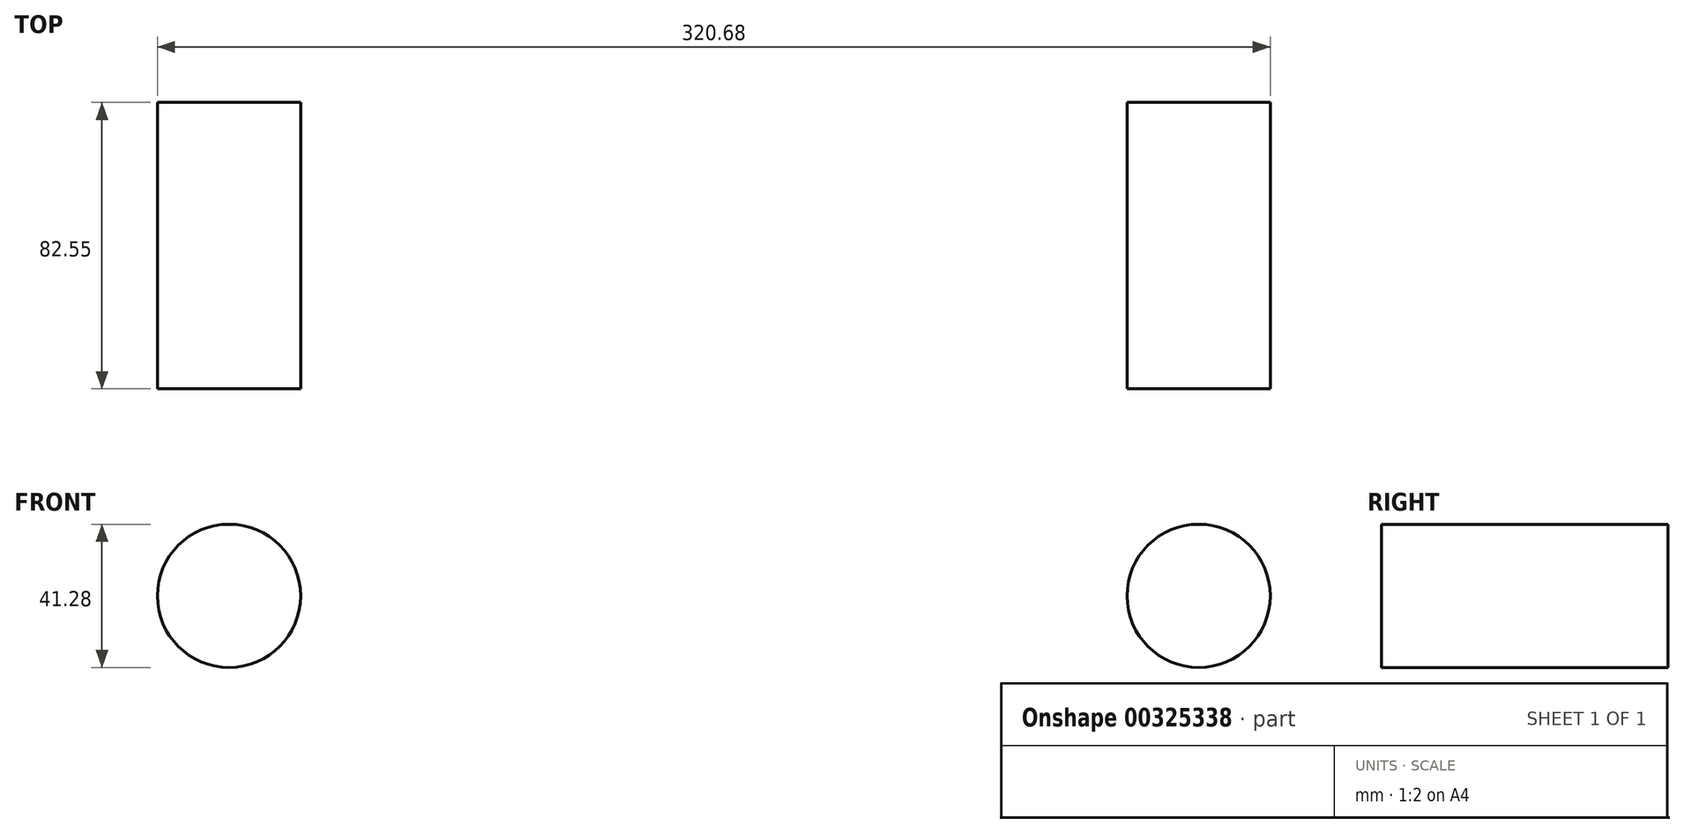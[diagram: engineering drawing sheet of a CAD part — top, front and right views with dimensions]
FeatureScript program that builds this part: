
annotation { "Feature Type Name" : "Feature", "Feature Type Description" : "" }
export const myFeature = defineFeature(function(context is Context, id is Id, definition is map)
    precondition{}
    {
        {
            var Q0;
            Q0=qCreatedBy(makeId("Top.planeOp"),FACE);
            var sketch = newSketch(context, id + "F0", { "sketchPlane" : qUnion([Q0])});
            skLineSegment(sketch, "E0", {"start": v(279.4, -82.55) * mm, "end": v(279.4, 0) * mm});
            skLineSegment(sketch, "E1", {"start": v(0, -82.55) * mm, "end": v(0, 0) * mm});
            skLineSegment(sketch, "E2.bottom", {"start": v(33.02, 67.89) * mm, "end": v(248.92, 67.89) * mm});
            skLineSegment(sketch, "E2.top", {"start": v(33.02, -100.77) * mm, "end": v(248.92, -100.77) * mm});
            skLineSegment(sketch, "E2.left", {"start": v(33.02, 67.89) * mm, "end": v(33.02, -100.77) * mm});
            skLineSegment(sketch, "E2.right", {"start": v(248.92, 67.89) * mm, "end": v(248.92, -100.77) * mm});
            skLineSegment(sketch, "E3.bottom", {"start": v(77.47, -367.47) * mm, "end": v(204.47, -367.47) * mm});
            skLineSegment(sketch, "E3.top", {"start": v(77.47, -549.3) * mm, "end": v(204.47, -549.3) * mm});
            skLineSegment(sketch, "E3.left", {"start": v(77.47, -367.47) * mm, "end": v(77.47, -549.3) * mm});
            skLineSegment(sketch, "E3.right", {"start": v(204.47, -367.47) * mm, "end": v(204.47, -549.3) * mm});
            skArc(sketch, "E4", {"start": v(279.4, -82.55) * mm, "mid": v(262.43, -125.76) * mm, "end": v(220.6, -145.88) * mm});
            skArc(sketch, "E5", {"start": v(141.02, -300.99) * mm, "mid": v(120.83, -342.67) * mm, "end": v(77.7, -359.56) * mm});
            skLineSegment(sketch, "E6", {"start": v(77.7, -359.56) * mm, "end": v(65, -359.56) * mm});
            skArc(sketch, "E7", {"start": v(65, -359.56) * mm, "mid": v(20.1, -378.16) * mm, "end": v(1.5, -423.06) * mm});
            skArc(sketch, "E8", {"start": v(0, -82.55) * mm, "mid": v(16.97, -125.76) * mm, "end": v(58.8, -145.88) * mm});
            skArc(sketch, "E9", {"start": v(58.8, -145.88) * mm, "mid": v(97.15, -162.52) * mm, "end": v(116.84, -199.39) * mm});
            skLineSegment(sketch, "E10", {"start": v(1.5, -423.06) * mm, "end": v(1.5, -486.56) * mm});
            skPoint(sketch, "E11", {"position": v(140.97, 67.89) * mm});
            skPoint(sketch, "E12", {"position": v(140.97, -549.3) * mm});
            skLineSegment(sketch, "E13.bottom", {"start": v(-19.05, 53.76) * mm, "end": v(19.05, 53.76) * mm});
            skLineSegment(sketch, "E13.top", {"start": v(-19.05, -37.27) * mm, "end": v(19.05, -37.27) * mm});
            skLineSegment(sketch, "E13.left", {"start": v(-19.05, 53.76) * mm, "end": v(-19.05, -37.27) * mm});
            skLineSegment(sketch, "E13.right", {"start": v(19.05, 53.76) * mm, "end": v(19.05, -37.27) * mm});
            skPoint(sketch, "E14", {"position": v(0, 53.76) * mm});
            skLineSegment(sketch, "E15.bottom", {"start": v(260.35, 52.8) * mm, "end": v(298.45, 52.8) * mm});
            skLineSegment(sketch, "E15.top", {"start": v(260.35, -49.97) * mm, "end": v(298.45, -49.97) * mm});
            skLineSegment(sketch, "E15.left", {"start": v(260.35, 52.8) * mm, "end": v(260.35, -49.97) * mm});
            skLineSegment(sketch, "E15.right", {"start": v(298.45, 52.8) * mm, "end": v(298.45, -49.97) * mm});
            skPoint(sketch, "E16", {"position": v(279.4, 52.8) * mm});
            skArc(sketch, "E17", {"start": v(220.6, -145.88) * mm, "mid": v(182.25, -162.52) * mm, "end": v(162.56, -199.39) * mm});
            skFitSpline(sketch, "E18", {"points": [v(162.56, -199.39) * mm, v(141.02, -300.99) * mm], "startDerivative": vector(0, -96.27) * mm, "endDerivative": vector(0, -131.84) * mm});
            skFitSpline(sketch, "E19", {"points": [v(116.84, -199.39) * mm, v(141.02, -300.99) * mm], "startDerivative": vector(0, -90.14) * mm, "endDerivative": vector(0, -131.84) * mm});
            skSolve(sketch);
        }
        {
            var Q0;
            Q0=qCreatedBy(makeId("Front.planeOp"),FACE);
            var sketch = newSketch(context, id + "F1", { "sketchPlane" : qUnion([Q0])});
            skCircle(sketch, "E20", {"center": v(279.4, 0) * mm, "radius": 20.64 * mm});
            skCircle(sketch, "E21", {"center": v(0, 0) * mm, "radius": 20.64 * mm});
            skSolve(sketch);
        }
        {
            var Q0;
            Q0=qSketchRegion(id+"F1",true);
            var Q1;
            Q1=sQuery(id+"F1.wireOp",EDGE,"E20");
            var Q2;
            Q2=sQuery(id+"F0.wireOp",EDGE,"E0");
            sweep(context, id + "F2", {"bodyType" : ToolBodyType.SURFACE, "profiles" : qUnion([Q0]), "surfaceProfiles" : qUnion([Q1]), "path" : qUnion([Q2])});
        }
        {
            var Q0;
            Q0=qSketchRegion(id+"F1",true);
            var Q1;
            Q1=sQuery(id+"F1.wireOp",EDGE,"E21");
            var Q2;
            Q2=sQuery(id+"F0.wireOp",EDGE,"E1");
            sweep(context, id + "F3", {"bodyType" : ToolBodyType.SURFACE, "profiles" : qUnion([Q0]), "surfaceProfiles" : qUnion([Q1]), "path" : qUnion([Q2])});
        }
    });
